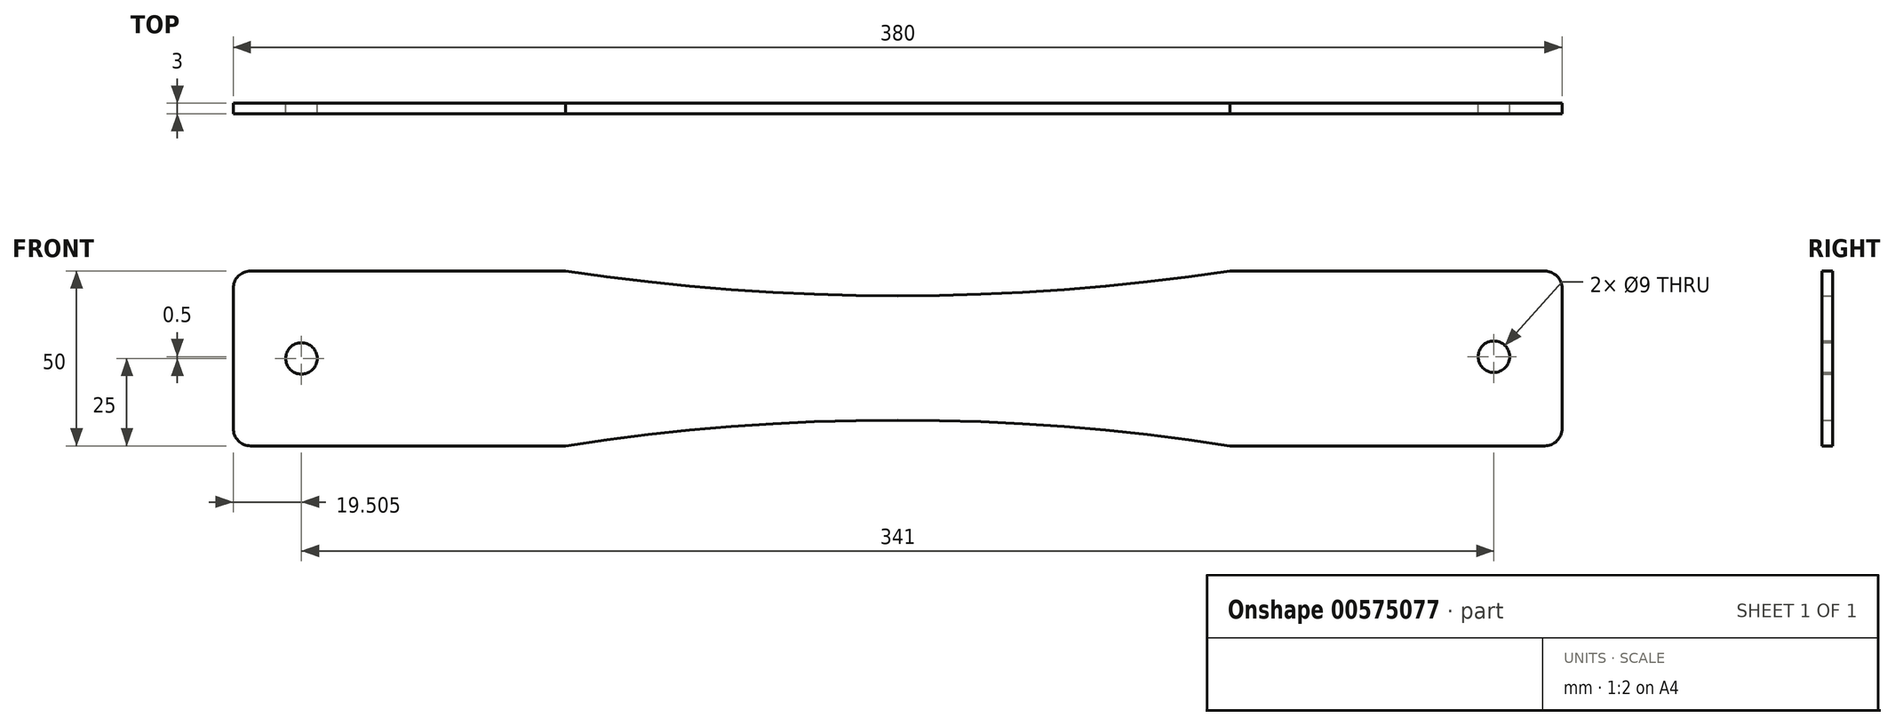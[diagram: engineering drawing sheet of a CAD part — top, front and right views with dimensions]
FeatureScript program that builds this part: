
annotation { "Feature Type Name" : "Feature", "Feature Type Description" : "" }
export const myFeature = defineFeature(function(context is Context, id is Id, definition is map)
    precondition{}
    {
        {
            var Q0;
            Q0=qCreatedBy(makeId("Front.planeOp"),FACE);
            var sketch = newSketch(context, id + "F0", { "sketchPlane" : qUnion([Q0])});
            skLineSegment(sketch, "E0.bottom", {"start": v(-198.39, -19.7) * mm, "end": v(-108.39, -19.7) * mm});
            skLineSegment(sketch, "E0.top", {"start": v(-198.39, -69.7) * mm, "end": v(-108.39, -69.7) * mm});
            skLineSegment(sketch, "E0.left", {"start": v(-203.39, -24.7) * mm, "end": v(-203.39, -64.7) * mm});
            skLineSegment(sketch, "E0.right", {"start": v(176.61, -24.7) * mm, "end": v(176.61, -64.7) * mm});
            skCircle(sketch, "E1", {"center": v(-183.89, -44.7) * mm, "radius": 4.5 * mm});
            skCircle(sketch, "E2", {"center": v(157.11, -44.2) * mm, "radius": 4.5 * mm});
            skLineSegment(sketch, "E3", {"start": v(-108.39, 18.9) * mm, "end": v(-108.39, -95.66) * mm, "construction": true});
            skLineSegment(sketch, "E4", {"start": v(81.61, 15.4) * mm, "end": v(81.61, -94.49) * mm, "construction": true});
            skArc(sketch, "E5", {"start": v(-108.39, -19.7) * mm, "mid": v(-13.39, -26.81) * mm, "end": v(81.61, -19.7) * mm});
            skArc(sketch, "E6", {"start": v(81.61, -69.7) * mm, "mid": v(-13.39, -62.34) * mm, "end": v(-108.39, -69.7) * mm});
            skLineSegment(sketch, "E7.trimOffspring", {"start": v(81.61, -19.7) * mm, "end": v(171.61, -19.7) * mm});
            skLineSegment(sketch, "E8.trimOffspring", {"start": v(81.61, -69.7) * mm, "end": v(171.61, -69.7) * mm});
            skPoint(sketch, "E9.visualSharp", {"position": v(-203.39, -19.7) * mm});
            skArc(sketch, "E9.filletArc", {"start": v(-198.39, -19.7) * mm, "mid": v(-201.92, -21.16) * mm, "end": v(-203.39, -24.7) * mm});
            skPoint(sketch, "E10.visualSharp", {"position": v(-203.39, -69.7) * mm});
            skArc(sketch, "E10.filletArc", {"start": v(-203.39, -64.7) * mm, "mid": v(-201.92, -68.24) * mm, "end": v(-198.39, -69.7) * mm});
            skPoint(sketch, "E11.visualSharp", {"position": v(176.61, -19.7) * mm});
            skArc(sketch, "E11.filletArc", {"start": v(176.61, -24.7) * mm, "mid": v(175.15, -21.16) * mm, "end": v(171.61, -19.7) * mm});
            skPoint(sketch, "E12.visualSharp", {"position": v(176.61, -69.7) * mm});
            skArc(sketch, "E12.filletArc", {"start": v(171.61, -69.7) * mm, "mid": v(175.15, -68.24) * mm, "end": v(176.61, -64.7) * mm});
            skSolve(sketch);
        }
        {
            var Q0;
            Q0 = qSketchRegion(id + "F0", true);
            extrude(context, id + "F1", {"entities" : qUnion([Q0]), "depth" : 3 * mm, "offsetDistance" : 25 * mm});
        }
    });
